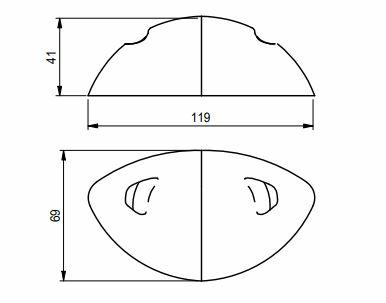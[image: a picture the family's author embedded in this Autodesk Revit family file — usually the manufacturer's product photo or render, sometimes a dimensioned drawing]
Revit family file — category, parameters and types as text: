
# Revit family: R-MBD-494
name_source: partatom
category: Portes
units: mm (PartAtom-declared; Revit-internal decimal feet)

## family parameters
Couper avec des vides une fois chargée = Non
Hôte = Mur
Partagée = Non
Repère de localisation dans la pièce = Oui
Toujours verticalement = Oui

## types (1)
- MBD-494
    1 Vantail = Non
    2 Vantaux = Oui
    A.E.V = non
    Acoustique = non
    Anti-Effraction = non
    Certification = D.A.S. Mode 2 certifié NF
    Code_MAJ = 2303130305MBD494
    Coloris_Chants = BER
    Coloris_Dormant = Hêtre
    Coloris_Face_Cote_Oppose_Ouverture = Prépeint
    Coloris_Face_Cote_Ouverture = Prépeint
    Construction analytique = <Aucun>
    DAS = Oui
    DC Larg Feuillure = 12 mm  [stored 0.0393701 ft]
    DC Pivot Vantail = 60 mm  [stored 0.19685 ft]
    Description = Bloc-porte bois D.A.S. 2 vantaux SP51 avec pivots linteaux motorisés encastrés, double action / va-et-vient, EI60, D.A.S. certifié NF, sur huisserie bois sans montant avec fileur
    Définir les propriétés thermiques par = Type schématique
    Ep Profil Pose Tunnel = 118 mm
    Ep Strat Vantail = 1 mm  [stored 0.00328084 ft]
    Ep Vantail = 51 mm  [stored 0.167323 ft]
    Epaisseur_Rainure à brique = 8 mm  [stored 0.0262467 ft]
    Fabricant = MALERBA
    Fiche_Produit = MBD-494
    Fileur = Oui
    Hauteur_Tableau = 2125 mm
    Hauteur_Vantaux_Souhaitée = 2040 mm  [stored 6.69291 ft]
    Jeu_1 = 0 mm  [stored 0 ft]
    Jeu_2 = 0 mm  [stored 0 ft]
    Jeu_Côté_Articulation_Vantail = 8 mm  [stored 0.0262467 ft]
    Jeu_Côté_Fermeture_Vantail = 8 mm  [stored 0.0262467 ft]
    Jeu_Haut = 3 mm  [stored 0.00984252 ft]
    Larg Profil = 58 mm  [stored 0.190289 ft]
    Larg Profil Avec Fileur = 20 mm  [stored 0.0656168 ft]
    Larg Profil Trav = 76 mm  [stored 0.249344 ft]
    Largeur = 0 mm  [stored 0 ft]
    Largeur_Vantail_Semi_Fixe_Souhaitée = 930 mm  [stored 3.05118 ft]
    Largeur_Vantail_Service_Souhaitée = 930 mm  [stored 3.05118 ft]
    Mat APD = Caoutchouc noir
    Mat Parclose = BER 2
    Mat Parclose Métal = Peinture Laquée PMT - Blanc Pur - RAL 9010
    Materiaux_Dominant = Bois
    Modèle = Va et vient
    Montant_VV = Non
    Note d'identification = 2V EI60/SP51 DAS - LINTEAU MOTORISE - SANS MONTANT AVEC FILEUR
    Pivot linteau motorisé = Oui
    Profondeur_Rainure à brique = 5 mm  [stored 0.0164042 ft]
    Reference_Commerciale = 2V SP51/DA LINTEAU OP
    Resistance_Feu = EI30
    Sans_Montants = Non
    Sens_Feu = Recto / Verso
    Thermique (W/m2.°K) = 0
    URL = https://www.malerba.fr
    X_Axe Pivot = 88 mm  [stored 0.288714 ft]
    X_DC seuil = 9 mm  [stored 0.0295276 ft]
    X_Inv_DC Larg Feuillure_1V Montant = 0 mm  [stored 0 ft]

note: [stored X ft] marks values corroborated as IEEE doubles in the binary element streams (Revit-internal decimal feet)

## geometry (parser evidence)
native form markers: Blend x14
no freeform markers — native parametric forms only
